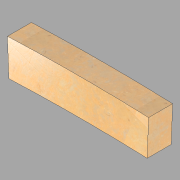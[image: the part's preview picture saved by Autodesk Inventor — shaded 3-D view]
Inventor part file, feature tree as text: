
AUTODESK INVENTOR PART (.ipt)
format: ipt  version: 2022.1 (Build 261234020, 234B)  size: 108,544 bytes
history: imported  units: in
note: dims shown in document units (in); Inventor stores cm internally (conversion verified against a paired STEP export)
features: imported_body x1
ambient origin geometry x8: Origin, YZ Plane, XZ Plane, XY Plane, X Axis, Y Axis, Z Axis, Center Point
bodies: Solid1 (imported_parasolid), Body1 (imported_parasolid)
feature tree (1):
  imported_body  NMx_Import_Brep_tag  [imported B-rep: ~6 faces, bbox_mm=[896.501222, 229.790027, 152.4]]
